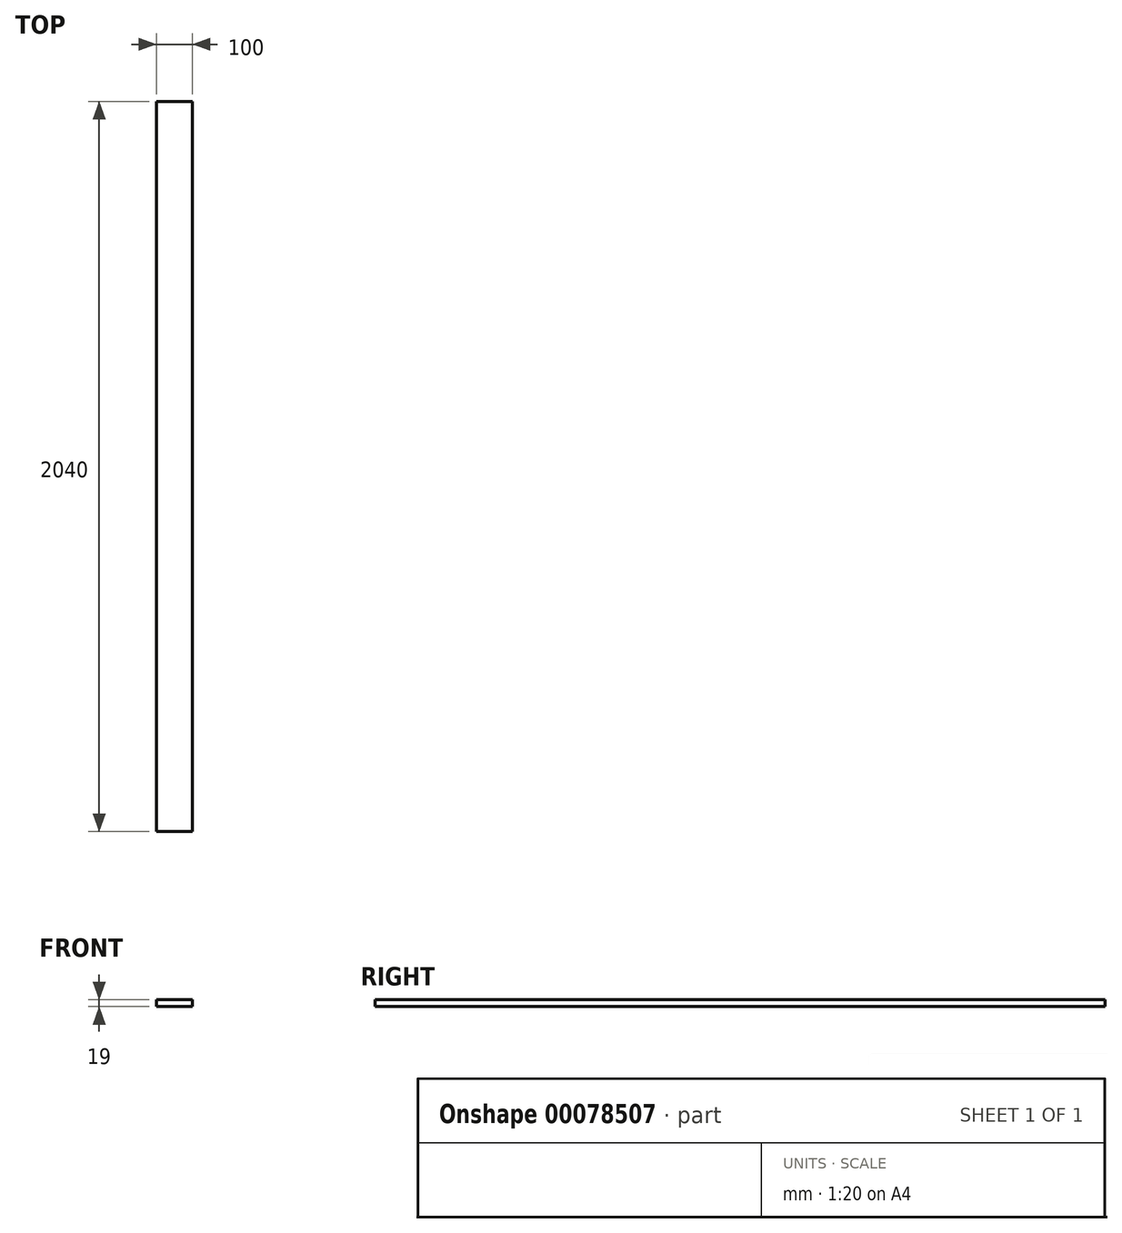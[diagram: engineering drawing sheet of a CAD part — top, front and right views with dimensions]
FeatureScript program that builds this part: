
annotation { "Feature Type Name" : "Feature", "Feature Type Description" : "" }
export const myFeature = defineFeature(function(context is Context, id is Id, definition is map)
    precondition{}
    {
        {
            var Q0;
            Q0=qCreatedBy(makeId("Front.planeOp"),FACE);
            var sketch = newSketch(context, id + "F0", { "sketchPlane" : qUnion([Q0])});
            skLineSegment(sketch, "E0.bottom", {"start": v(50, -9.5) * mm, "end": v(-50, -9.5) * mm});
            skLineSegment(sketch, "E0.top", {"start": v(50, 9.5) * mm, "end": v(-50, 9.5) * mm});
            skLineSegment(sketch, "E0.left", {"start": v(50, -9.5) * mm, "end": v(50, 9.5) * mm});
            skLineSegment(sketch, "E0.right", {"start": v(-50, -9.5) * mm, "end": v(-50, 9.5) * mm});
            skPoint(sketch, "E0.middle", {"position": v(0, 0) * mm});
            skSolve(sketch);
        }
        {
            var Q0;
            Q0 = qSketchRegion(id + "F0", true);
            extrude(context, id + "F1", {"entities" : qUnion([Q0]), "endBound" : BoundingType.SYMMETRIC, "depth" : (1650 + 390) * mm});
        }
    });
